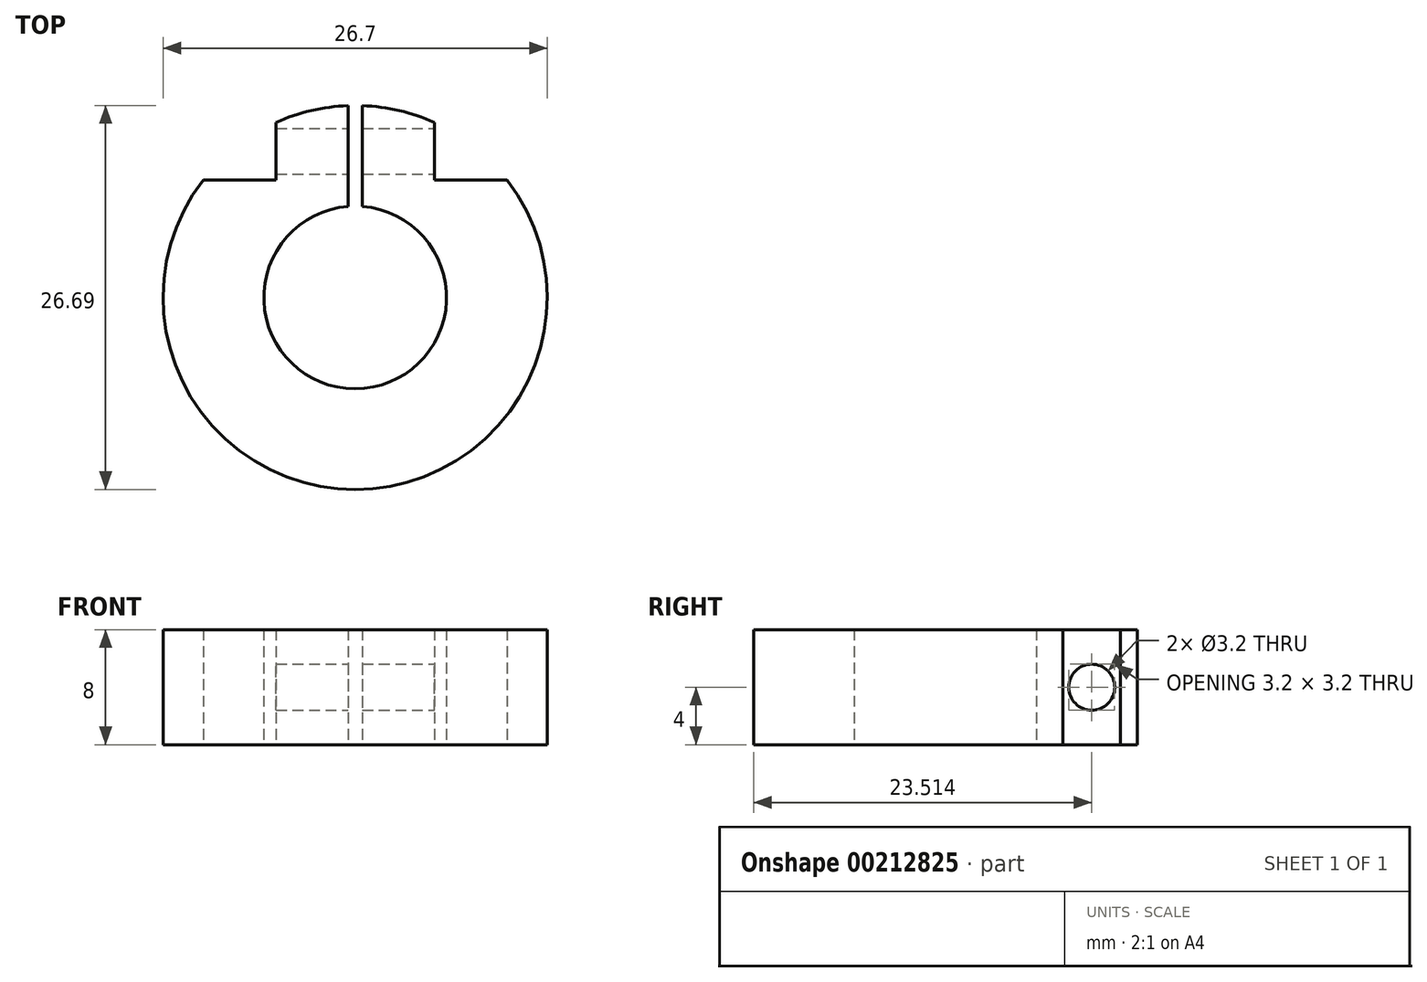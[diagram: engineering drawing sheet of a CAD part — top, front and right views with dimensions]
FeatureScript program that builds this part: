
annotation { "Feature Type Name" : "Feature", "Feature Type Description" : "" }
export const myFeature = defineFeature(function(context is Context, id is Id, definition is map)
    precondition{}
    {
        {
            var Q0;
            Q0=qCreatedBy(makeId("Top.planeOp"),FACE);
            var sketch = newSketch(context, id + "F0", { "sketchPlane" : qUnion([Q0])});
            skArc(sketch, "E0", {"start": v(-0.5, 6.33) * mm, "mid": v(0, -6.35) * mm, "end": v(0.5, 6.33) * mm});
            skArc(sketch, "E1", {"start": v(-10.56, 8.16) * mm, "mid": v(0, -13.35) * mm, "end": v(10.56, 8.16) * mm});
            skLineSegment(sketch, "E2", {"start": v(-0.5, 6.33) * mm, "end": v(-0.5, 13.34) * mm});
            skLineSegment(sketch, "E3", {"start": v(0.5, 6.33) * mm, "end": v(0.5, 13.34) * mm});
            skLineSegment(sketch, "E4", {"start": v(0, 13.35) * mm, "end": v(0, 6.35) * mm, "construction": true});
            skLineSegment(sketch, "E5", {"start": v(5.5, 12.16) * mm, "end": v(5.5, 8.16) * mm});
            skLineSegment(sketch, "E6", {"start": v(5.5, 8.16) * mm, "end": v(10.56, 8.16) * mm});
            skLineSegment(sketch, "E7", {"start": v(-5.5, 12.16) * mm, "end": v(-5.5, 8.16) * mm});
            skLineSegment(sketch, "E8", {"start": v(-5.5, 8.16) * mm, "end": v(-10.56, 8.16) * mm});
            skArc(sketch, "E9.trimOffspring", {"start": v(5.5, 12.16) * mm, "mid": v(3.06, 13) * mm, "end": v(0.5, 13.34) * mm});
            skArc(sketch, "E10.trimOffspring", {"start": v(-0.5, 13.34) * mm, "mid": v(-3.06, 13) * mm, "end": v(-5.5, 12.16) * mm});
            skSolve(sketch);
        }
        {
            var Q0;
            Q0=makeQuery(id+"F0.imprint","IMPRINT",FACE,{"disambiguationData":[TD([[makeQuery(id+"F0.imprint","IMPRINT",EDGE,{"derivedFrom":sQuery(id+"F0.wireOp",EDGE,"E0")}),-1.0]])]});
            extrude(context, id + "F1", {"entities" : qUnion([Q0]), "depth" : 8 * mm});
        }
        {
            var Q0;
            Q0=makeQuery(id+"F1.opExtrude","SWEPT_FACE",FACE,{"disambiguationData":[OSD([sQuery(id+"F0.wireOp",EDGE,"E5")])]});
            var sketch = newSketch(context, id + "F2", { "sketchPlane" : qUnion([Q0])});
            skCircle(sketch, "E11", {"center": v(10.16, 4) * mm, "radius": 1.6 * mm});
            skLineSegment(sketch, "E12", {"start": v(8.16, 0) * mm, "end": v(12.16, 0) * mm, "construction": true});
            skLineSegment(sketch, "E13", {"start": v(8.16, 8) * mm, "end": v(12.16, 8) * mm, "construction": true});
            skPoint(sketch, "E14", {"position": v(10.16, 8) * mm});
            skPoint(sketch, "E15", {"position": v(10.16, 0) * mm});
            skSolve(sketch);
        }
        {
            var Q0;
            Q0=makeQuery(id+"F2.imprint","IMPRINT",FACE,{"disambiguationData":[TD([[makeQuery(id+"F2.imprint","IMPRINT",EDGE,{"derivedFrom":sQuery(id+"F2.wireOp",EDGE,"E11")}),1.0]])]});
            extrude(context, id + "F3", {"entities" : qUnion([Q0]), "operationType" : NewBodyOperationType.REMOVE, "oppositeDirection" : true, "depth" : 25.4 * mm});
        }
    });
